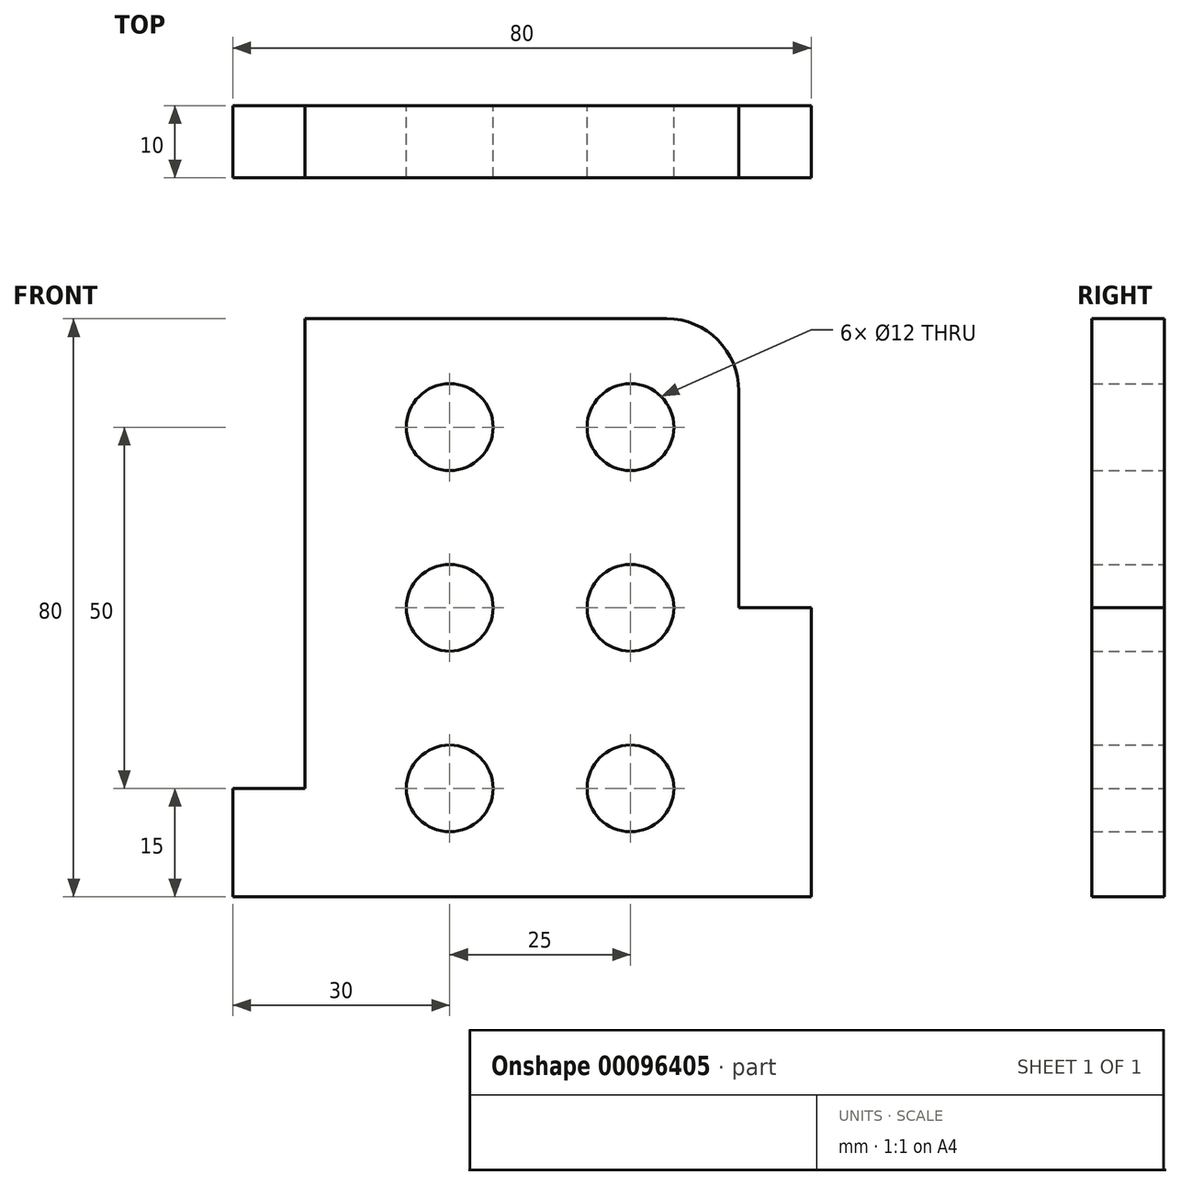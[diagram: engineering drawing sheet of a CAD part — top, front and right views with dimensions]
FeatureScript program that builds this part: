
annotation { "Feature Type Name" : "Feature", "Feature Type Description" : "" }
export const myFeature = defineFeature(function(context is Context, id is Id, definition is map)
    precondition{}
    {
        {
            var Q0;
            Q0=qCreatedBy(makeId("Front.planeOp"),FACE);
            var sketch = newSketch(context, id + "F0", { "sketchPlane" : qUnion([Q0])});
            skLineSegment(sketch, "E0", {"start": v(0, 0) * mm, "end": v(80, 0) * mm});
            skLineSegment(sketch, "E1", {"start": v(80, 0) * mm, "end": v(80, 40) * mm});
            skLineSegment(sketch, "E2", {"start": v(80, 40) * mm, "end": v(70, 40) * mm});
            skLineSegment(sketch, "E3", {"start": v(70, 40) * mm, "end": v(70, 70) * mm});
            skLineSegment(sketch, "E4", {"start": v(60, 80) * mm, "end": v(10, 80) * mm});
            skLineSegment(sketch, "E5", {"start": v(10, 80) * mm, "end": v(10, 15) * mm});
            skLineSegment(sketch, "E6", {"start": v(10, 15) * mm, "end": v(0, 15) * mm});
            skLineSegment(sketch, "E7", {"start": v(0, 15) * mm, "end": v(0, 0) * mm});
            skPoint(sketch, "E8.visualSharp", {"position": v(70, 80) * mm});
            skArc(sketch, "E8.filletArc", {"start": v(70, 70) * mm, "mid": v(67.07, 77.07) * mm, "end": v(60, 80) * mm});
            skCircle(sketch, "E9", {"center": v(30, 15) * mm, "radius": 6 * mm});
            skCircle(sketch, "E10", {"center": v(30, 40) * mm, "radius": 6 * mm});
            skCircle(sketch, "E11", {"center": v(30, 65) * mm, "radius": 6 * mm});
            skCircle(sketch, "E12", {"center": v(55, 15) * mm, "radius": 6 * mm});
            skCircle(sketch, "E13", {"center": v(55, 40) * mm, "radius": 6 * mm});
            skCircle(sketch, "E14", {"center": v(55, 65) * mm, "radius": 6 * mm});
            skLineSegment(sketch, "E15", {"start": v(55, 65) * mm, "end": v(55, 15) * mm, "construction": true});
            skSolve(sketch);
        }
        {
            var Q0;
            Q0 = qSketchRegion(id + "F0", true);
            extrude(context, id + "F1", {"entities" : qUnion([Q0]), "depth" : 10 * mm});
        }
    });
